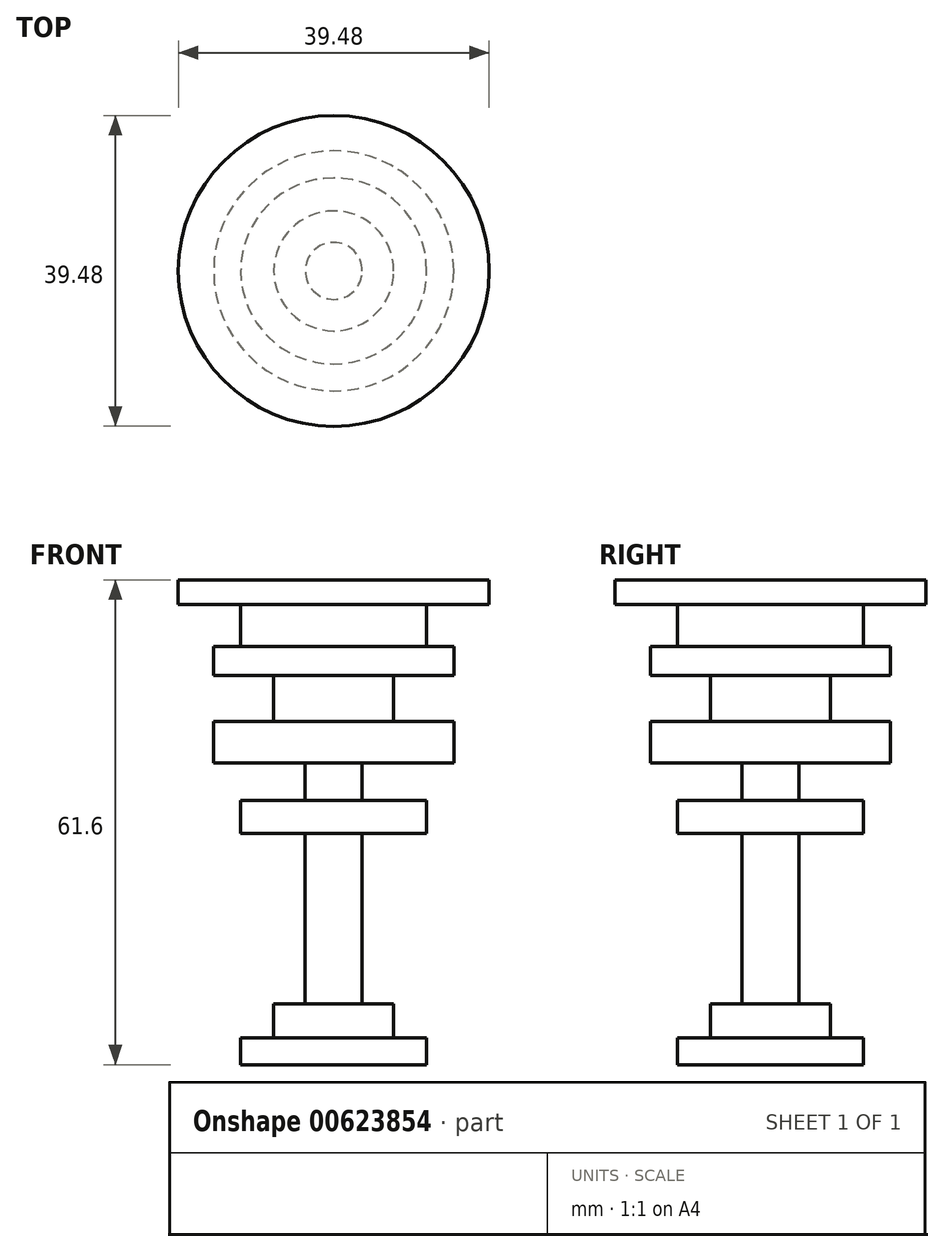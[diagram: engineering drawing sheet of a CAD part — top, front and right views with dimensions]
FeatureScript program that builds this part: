
annotation { "Feature Type Name" : "Feature", "Feature Type Description" : "" }
export const myFeature = defineFeature(function(context is Context, id is Id, definition is map)
    precondition{}
    {
        {
            var Q0;
            Q0=qCreatedBy(makeId("Front.planeOp"),FACE);
            var sketch = newSketch(context, id + "F0", { "sketchPlane" : qUnion([Q0])});
            skLineSegment(sketch, "E0.bottom", {"start": v(0, 53.86) * mm, "end": v(-19.74, 53.86) * mm});
            skLineSegment(sketch, "E0.top", {"start": v(0, 50.69) * mm, "end": v(-19.74, 50.69) * mm});
            skLineSegment(sketch, "E0.left", {"start": v(0, 53.86) * mm, "end": v(0, 50.69) * mm});
            skLineSegment(sketch, "E0.right", {"start": v(-19.74, 53.86) * mm, "end": v(-19.74, 50.69) * mm});
            skLineSegment(sketch, "E1.bottom", {"start": v(0, 50.69) * mm, "end": v(-11.81, 50.69) * mm});
            skLineSegment(sketch, "E1.top", {"start": v(0, 45.4) * mm, "end": v(-11.81, 45.4) * mm});
            skLineSegment(sketch, "E1.left", {"start": v(0, 50.69) * mm, "end": v(0, 45.4) * mm});
            skLineSegment(sketch, "E1.right", {"start": v(-11.81, 50.69) * mm, "end": v(-11.81, 45.4) * mm});
            skLineSegment(sketch, "E2.bottom", {"start": v(0, 45.4) * mm, "end": v(-15.25, 45.4) * mm});
            skLineSegment(sketch, "E2.top", {"start": v(0, 41.7) * mm, "end": v(-15.25, 41.7) * mm});
            skLineSegment(sketch, "E2.left", {"start": v(0, 45.4) * mm, "end": v(0, 41.7) * mm});
            skLineSegment(sketch, "E2.right", {"start": v(-15.25, 45.4) * mm, "end": v(-15.25, 41.7) * mm});
            skPoint(sketch, "E3.oppositeSnap0", {"position": v(-7.62, 41.7) * mm});
            skLineSegment(sketch, "E3.bottom", {"start": v(0, 41.7) * mm, "end": v(-7.62, 41.7) * mm});
            skLineSegment(sketch, "E3.top", {"start": v(0, 35.88) * mm, "end": v(-7.62, 35.88) * mm});
            skLineSegment(sketch, "E3.left", {"start": v(0, 41.7) * mm, "end": v(0, 35.88) * mm});
            skLineSegment(sketch, "E3.right", {"start": v(-7.62, 41.7) * mm, "end": v(-7.62, 35.88) * mm});
            skLineSegment(sketch, "E4.bottom", {"start": v(0, 35.88) * mm, "end": v(-15.25, 35.88) * mm});
            skLineSegment(sketch, "E4.top", {"start": v(0, 30.6) * mm, "end": v(-15.25, 30.6) * mm});
            skLineSegment(sketch, "E4.left", {"start": v(0, 35.88) * mm, "end": v(0, 30.6) * mm});
            skLineSegment(sketch, "E4.right", {"start": v(-15.25, 35.88) * mm, "end": v(-15.25, 30.6) * mm});
            skLineSegment(sketch, "E5.bottom", {"start": v(0, 30.6) * mm, "end": v(-3.62, 30.6) * mm});
            skLineSegment(sketch, "E5.top", {"start": v(0, 25.83) * mm, "end": v(-3.62, 25.83) * mm});
            skLineSegment(sketch, "E5.left", {"start": v(0, 30.6) * mm, "end": v(0, 25.83) * mm});
            skLineSegment(sketch, "E5.right", {"start": v(-3.62, 30.6) * mm, "end": v(-3.62, 25.83) * mm});
            skLineSegment(sketch, "E6.bottom", {"start": v(0, 25.83) * mm, "end": v(-11.81, 25.83) * mm});
            skLineSegment(sketch, "E6.top", {"start": v(0, 21.6) * mm, "end": v(-11.81, 21.6) * mm});
            skLineSegment(sketch, "E6.left", {"start": v(0, 25.83) * mm, "end": v(0, 21.6) * mm});
            skLineSegment(sketch, "E6.right", {"start": v(-11.81, 25.83) * mm, "end": v(-11.81, 21.6) * mm});
            skLineSegment(sketch, "E7.bottom", {"start": v(0, 21.6) * mm, "end": v(-3.62, 21.6) * mm});
            skLineSegment(sketch, "E7.top", {"start": v(0, 0) * mm, "end": v(-3.62, 0) * mm});
            skLineSegment(sketch, "E7.left", {"start": v(0, 21.6) * mm, "end": v(0, 0) * mm});
            skLineSegment(sketch, "E7.right", {"start": v(-3.62, 21.6) * mm, "end": v(-3.62, 0) * mm});
            skLineSegment(sketch, "E8.bottom", {"start": v(0, 0) * mm, "end": v(-7.62, 0) * mm});
            skLineSegment(sketch, "E8.top", {"start": v(0, -4.3) * mm, "end": v(-7.62, -4.3) * mm});
            skLineSegment(sketch, "E8.left", {"start": v(0, 0) * mm, "end": v(0, -4.3) * mm});
            skLineSegment(sketch, "E8.right", {"start": v(-7.62, 0) * mm, "end": v(-7.62, -4.3) * mm});
            skLineSegment(sketch, "E9.bottom", {"start": v(0, -4.3) * mm, "end": v(-11.81, -4.3) * mm});
            skLineSegment(sketch, "E9.top", {"start": v(0, -7.74) * mm, "end": v(-11.81, -7.74) * mm});
            skLineSegment(sketch, "E9.left", {"start": v(0, -4.3) * mm, "end": v(0, -7.74) * mm});
            skLineSegment(sketch, "E9.right", {"start": v(-11.81, -4.3) * mm, "end": v(-11.81, -7.74) * mm});
            skSolve(sketch);
        }
        {
            var Q0;
            Q0 = qSketchRegion(id + "F0", true);
            var Q1;
            Q1=sQuery(id+"F0.wireOp",EDGE,"E7.left");
            revolve(context, id + "F1", {"entities" : qUnion([Q0]), "axis" : qUnion([Q1]), "revolveType" : RevolveType.FULL});
        }
    });
